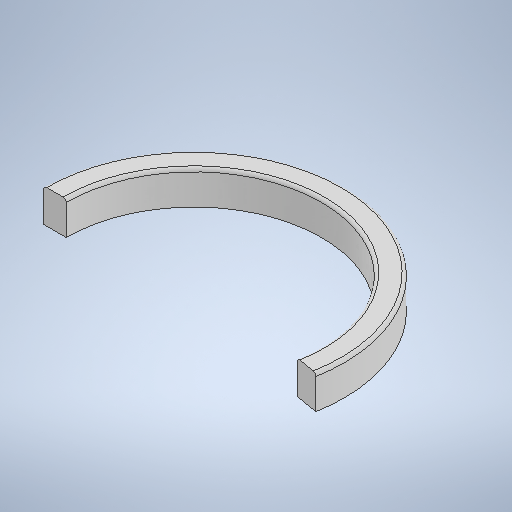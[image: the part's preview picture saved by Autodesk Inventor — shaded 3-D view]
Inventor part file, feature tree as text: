
AUTODESK INVENTOR PART (.ipt)
format: ipt  version: 2025 (Build 290162000, 162)  size: 255,488 bytes
history: native  units: in
note: dims shown in document units (in); Inventor stores cm internally (conversion verified against a paired STEP export)
features: revolve x1, sketch x1
ambient origin geometry x8: Origin, YZ Plane, XZ Plane, XY Plane, X Axis, Y Axis, Z Axis, Center Point
bodies: Solid1 (feature_tree)
feature tree (2):
  revolve  "Revolution1"  Angle=90.0deg
  sketch  "Sketch1"  dims[d0=0.8543in d1=90.0deg d2=0.2894in d3=0.5787in d4=0.0787in d5=3.5433in d6=1.3056in d7=0.0in]
